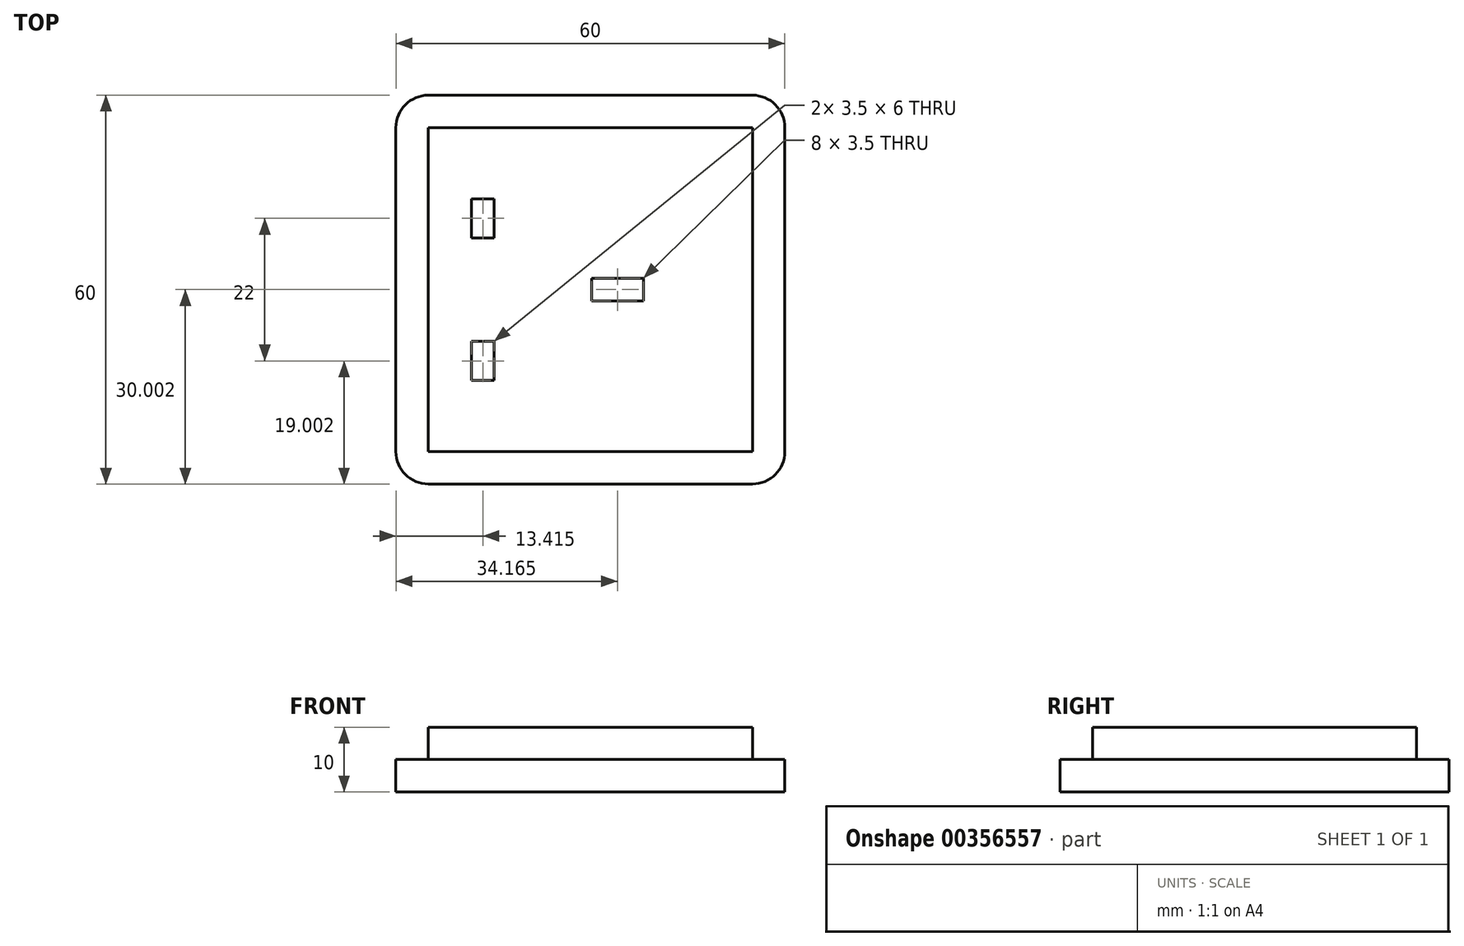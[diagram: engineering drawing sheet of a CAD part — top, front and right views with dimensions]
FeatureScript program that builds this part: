
annotation { "Feature Type Name" : "Feature", "Feature Type Description" : "" }
export const myFeature = defineFeature(function(context is Context, id is Id, definition is map)
    precondition{}
    {
        {
            var Q0;
            Q0=qCreatedBy(makeId("Top.planeOp"),FACE);
            var sketch = newSketch(context, id + "F0", { "sketchPlane" : qUnion([Q0])});
            skLineSegment(sketch, "E0.bottom", {"start": v(-27.55, 35.04) * mm, "end": v(22.45, 35.04) * mm});
            skLineSegment(sketch, "E0.top", {"start": v(-27.55, -24.96) * mm, "end": v(22.45, -24.96) * mm});
            skLineSegment(sketch, "E0.left", {"start": v(-32.55, 30.04) * mm, "end": v(-32.55, -19.96) * mm});
            skLineSegment(sketch, "E0.right", {"start": v(27.45, 30.04) * mm, "end": v(27.45, -19.96) * mm});
            skPoint(sketch, "E1.visualSharp", {"position": v(-32.55, 35.04) * mm});
            skArc(sketch, "E1.filletArc", {"start": v(-27.55, 35.04) * mm, "mid": v(-31.09, 33.58) * mm, "end": v(-32.55, 30.04) * mm});
            skPoint(sketch, "E2.visualSharp", {"position": v(27.45, 35.04) * mm});
            skArc(sketch, "E2.filletArc", {"start": v(27.45, 30.04) * mm, "mid": v(25.98, 33.58) * mm, "end": v(22.45, 35.04) * mm});
            skPoint(sketch, "E3.visualSharp", {"position": v(27.45, -24.96) * mm});
            skArc(sketch, "E3.filletArc", {"start": v(22.45, -24.96) * mm, "mid": v(25.98, -23.5) * mm, "end": v(27.45, -19.96) * mm});
            skPoint(sketch, "E4.visualSharp", {"position": v(-32.55, -24.96) * mm});
            skArc(sketch, "E4.filletArc", {"start": v(-32.55, -19.96) * mm, "mid": v(-31.09, -23.5) * mm, "end": v(-27.55, -24.96) * mm});
            skSolve(sketch);
        }
        {
            var Q0;
            Q0=makeQuery(id+"F0.imprint","IMPRINT",FACE,{"disambiguationData":[TD([[makeQuery(id+"F0.imprint","IMPRINT",EDGE,{"derivedFrom":sQuery(id+"F0.wireOp",EDGE,"E0.bottom")}),-1.0]])]});
            extrude(context, id + "F1", {"entities" : qUnion([Q0]), "depth" : 5 * mm});
        }
        {
            var Q0;
            Q0=makeQuery(id+"F1.opExtrude","CAP_FACE",FACE,{"disambiguationData":[OSD([sQuery(id+"F0.wireOp",EDGE,"E0.bottom"),sQuery(id+"F0.wireOp",EDGE,"E0.top"),sQuery(id+"F0.wireOp",EDGE,"E0.left"),sQuery(id+"F0.wireOp",EDGE,"E0.right"),sQuery(id+"F0.wireOp",EDGE,"E1.filletArc"),sQuery(id+"F0.wireOp",EDGE,"E2.filletArc"),sQuery(id+"F0.wireOp",EDGE,"E3.filletArc"),sQuery(id+"F0.wireOp",EDGE,"E4.filletArc")])],"isStart":false});
            var sketch = newSketch(context, id + "F2", { "sketchPlane" : qUnion([Q0])});
            skLineSegment(sketch, "E5.0.0", {"start": v(-27.55, -24.96) * mm, "end": v(22.45, -24.96) * mm});
            skLineSegment(sketch, "E5.0.2", {"start": v(22.45, -24.96) * mm, "end": v(-27.55, -24.96) * mm});
            skLineSegment(sketch, "E6.0.0", {"start": v(27.45, -19.96) * mm, "end": v(27.45, 30.04) * mm});
            skLineSegment(sketch, "E6.0.2", {"start": v(27.45, 30.04) * mm, "end": v(27.45, -19.96) * mm});
            skLineSegment(sketch, "E7.0.0", {"start": v(22.45, 35.04) * mm, "end": v(-27.55, 35.04) * mm});
            skLineSegment(sketch, "E7.0.2", {"start": v(-27.55, 35.04) * mm, "end": v(22.45, 35.04) * mm});
            skLineSegment(sketch, "E8.0.0", {"start": v(-32.55, 30.04) * mm, "end": v(-32.55, -19.96) * mm});
            skLineSegment(sketch, "E8.0.2", {"start": v(-32.55, -19.96) * mm, "end": v(-32.55, 30.04) * mm});
            skLineSegment(sketch, "E9.0", {"start": v(-27.55, 30.04) * mm, "end": v(-27.55, -19.96) * mm});
            skLineSegment(sketch, "E9.1", {"start": v(-27.55, 30.04) * mm, "end": v(-27.55, 30.04) * mm});
            skLineSegment(sketch, "E9.2", {"start": v(-27.55, -19.96) * mm, "end": v(-27.55, -19.96) * mm});
            skLineSegment(sketch, "E9.3", {"start": v(22.45, 30.04) * mm, "end": v(-27.55, 30.04) * mm});
            skLineSegment(sketch, "E9.4", {"start": v(-27.55, -19.96) * mm, "end": v(22.45, -19.96) * mm});
            skLineSegment(sketch, "E9.5", {"start": v(22.45, -19.96) * mm, "end": v(22.45, -19.96) * mm});
            skLineSegment(sketch, "E9.6", {"start": v(22.45, -19.96) * mm, "end": v(22.45, 30.04) * mm});
            skLineSegment(sketch, "E9.7", {"start": v(22.45, 30.04) * mm, "end": v(22.45, 30.04) * mm});
            skSolve(sketch);
        }
        {
            var Q0;
            Q0=makeQuery(id+"F2.imprint","IMPRINT",FACE,{"disambiguationData":[TD([[makeQuery(id+"F2.imprint","IMPRINT",EDGE,{"derivedFrom":sQuery(id+"F2.wireOp",EDGE,"E9.0")}),1.0]])]});
            extrude(context, id + "F3", {"entities" : qUnion([Q0]), "operationType" : NewBodyOperationType.ADD, "depth" : 5 * mm});
        }
        {
            var Q0;
            Q0=makeQuery(id+"F1.opExtrude","CAP_FACE",FACE,{"disambiguationData":[OSD([sQuery(id+"F0.wireOp",EDGE,"E0.bottom"),sQuery(id+"F0.wireOp",EDGE,"E0.top"),sQuery(id+"F0.wireOp",EDGE,"E0.left"),sQuery(id+"F0.wireOp",EDGE,"E0.right"),sQuery(id+"F0.wireOp",EDGE,"E1.filletArc"),sQuery(id+"F0.wireOp",EDGE,"E2.filletArc"),sQuery(id+"F0.wireOp",EDGE,"E3.filletArc"),sQuery(id+"F0.wireOp",EDGE,"E4.filletArc")])],"isStart":true});
            var sketch = newSketch(context, id + "F4", { "sketchPlane" : qUnion([Q0])});
            skLineSegment(sketch, "E10", {"start": v(27.45, -5.04) * mm, "end": v(-32.55, -5.04) * mm, "construction": true});
            skLineSegment(sketch, "E11.0", {"start": v(-17.38, 2.96) * mm, "end": v(-20.88, 2.96) * mm});
            skLineSegment(sketch, "E12.0", {"start": v(-17.38, 8.96) * mm, "end": v(-20.88, 8.96) * mm});
            skLineSegment(sketch, "E13", {"start": v(-20.88, 8.96) * mm, "end": v(-20.88, 2.96) * mm});
            skLineSegment(sketch, "E14.0", {"start": v(-17.38, 8.96) * mm, "end": v(-17.38, 2.96) * mm});
            skLineSegment(sketch, "E15.MirrorCS", {"start": v(-17.38, -13.04) * mm, "end": v(-20.88, -13.04) * mm});
            skLineSegment(sketch, "E16.MirrorCS", {"start": v(-20.88, -19.04) * mm, "end": v(-20.88, -13.04) * mm});
            skLineSegment(sketch, "E17.MirrorCS", {"start": v(-17.38, -19.04) * mm, "end": v(-20.88, -19.04) * mm});
            skLineSegment(sketch, "E18.MirrorCS", {"start": v(-17.38, -19.04) * mm, "end": v(-17.38, -13.04) * mm});
            skLineSegment(sketch, "E19", {"start": v(-2.38, -6.8) * mm, "end": v(-2.38, -5.04) * mm});
            skLineSegment(sketch, "E20.0", {"start": v(5.62, -6.8) * mm, "end": v(5.62, -5.04) * mm});
            skLineSegment(sketch, "E21.0", {"start": v(5.62, -6.8) * mm, "end": v(-2.38, -6.8) * mm});
            skLineSegment(sketch, "E22.MirrorCS", {"start": v(5.62, -3.3) * mm, "end": v(-2.38, -3.3) * mm});
            skLineSegment(sketch, "E23.MirrorCS", {"start": v(5.62, -3.3) * mm, "end": v(5.62, -5.04) * mm});
            skLineSegment(sketch, "E24.MirrorCS", {"start": v(-2.38, -3.3) * mm, "end": v(-2.38, -5.04) * mm});
            skSolve(sketch);
        }
        {
            var Q0;
            Q0=makeQuery(id+"F4.imprint","IMPRINT",FACE,{"disambiguationData":[TD([[makeQuery(id+"F4.imprint","IMPRINT",EDGE,{"derivedFrom":sQuery(id+"F4.wireOp",EDGE,"E19")}),-1.0]])]});
            var Q1;
            Q1=makeQuery(id+"F4.imprint","IMPRINT",FACE,{"disambiguationData":[TD([[makeQuery(id+"F4.imprint","IMPRINT",EDGE,{"derivedFrom":sQuery(id+"F4.wireOp",EDGE,"E11.0")}),-1.0]])]});
            var Q2;
            Q2=makeQuery(id+"F4.imprint","IMPRINT",FACE,{"disambiguationData":[TD([[makeQuery(id+"F4.imprint","IMPRINT",EDGE,{"derivedFrom":sQuery(id+"F4.wireOp",EDGE,"E15.MirrorCS")}),1.0]])]});
            extrude(context, id + "F5", {"entities" : qUnion([Q0, Q1, Q2]), "operationType" : NewBodyOperationType.REMOVE, "oppositeDirection" : true, "depth" : 25 * mm});
        }
    });
